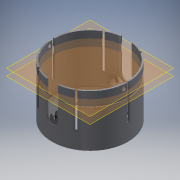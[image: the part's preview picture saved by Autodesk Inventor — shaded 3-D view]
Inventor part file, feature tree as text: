
AUTODESK INVENTOR PART (.ipt)
format: ipt  version: 2016 (Build 200138000, 138)  size: 449,024 bytes
history: native  units: mm
features: sketch x14, extrude x13, reference x8, plane x4, other x2, thicken_offset x2, mirror x1, pattern_circular x1, hole x1
ambient origin geometry x8: Origin, YZ Plane, XZ Plane, XY Plane, X Axis, Y Axis, Z Axis, Center Point
bodies: Solid1 (feature_tree)
feature tree (46):
  extrude  "Extrusion1"  Depth=4.0mm TaperAngle=0.0deg
  extrude  "Extrusion2"  Depth=4.0mm TaperAngle=0.0deg
  sketch  "Sketch3"  dims[d8=4.0mm d9=0.0mm d10=0.0mm d11=0.0mm]
  other  "Work Point1"
  extrude  "Extrusion3"  TaperAngle=0.0deg  [1 undecoded]
  extrude  "Extrusion4"  Depth=0.2mm
  extrude  "Extrusion5"  Depth=2.0mm
  plane  "Work Plane1"
  extrude  "Extrusion6"  Depth=1.0mm
  thicken_offset  "Thicken2"
  thicken_offset  "Thicken3"
  mirror  "Mirror1"
  extrude  "Extrusion7"  [1 undecoded]
  plane  "Work Plane2"
  extrude  "Extrusion8"  Depth=0.523599mm
  sketch  "Sketch9"  dims[d29=50.0mm d30=0.0mm d31=60.0mm d32=360.0deg]
  plane  "Work Plane3"
  plane  "Work Plane4"
  extrude  "Extrusion9"  Depth=60.0mm TaperAngle=360.0deg
  extrude  "Extrusion10"  Depth=50.0mm TaperAngle=0.0deg
  pattern_circular  "Circular Pattern1"  [2 undecoded]
  extrude  "Extrusion11"  Depth=3.0mm
  extrude  "Extrusion12"  Depth=3.0mm
  extrude  "Extrusion13"  Depth=3.0mm
  hole  "Hole1"  [1 undecoded]
  sketch  "Sketch1"  dims[d0=4.0mm d1=0.0mm d2=4.0mm d3=0.0mm]
  reference  "Reference1"
  reference  "Reference2"
  sketch  "Sketch2"  dims[d4=4.0mm d5=0.0mm d6=4.0mm d7=0.0mm]
  reference  "Reference3"
  reference  "Reference4"
  sketch  "Sketch4"  dims[d14=0.2mm d15=0.2mm d16=0.2mm d17=0.2mm]
  sketch  "Sketch5"  dims[d18=4.0mm d19=0.0mm d20=2.0mm]
  reference  "Reference6"
  sketch  "Sketch6"  dims[d21=70.0mm d22=0.0mm d23=1.0mm]
  reference  "Reference7"
  other  "Work Point2"
  sketch  "Sketch7"  dims[d24=-10.0mm d25=-20.0mm]
  sketch  "Sketch8"  dims[d26=70.0mm d27=0.0mm d28=0.523599mm]
  sketch  "Sketch10"  dims[d34=50.0mm d35=0.0mm d36=50.0mm d37=0.0mm]
  sketch  "Sketch11"  dims[d38=3.5mm]
  reference  "Reference8"
  sketch  "Sketch12"  dims[d39=0.0mm d40=0.0mm]
  reference  "Reference9"
  sketch  "Sketch13"  dims[d41=3.0mm]
  sketch  "Sketch14"  dims[d42=3.0mm d43=3.0mm d44=3.0mm d45=3.0mm d46=3.0mm d47=3.0mm d48=3.0mm d49=3.1mm d50=6.0mm d51=4.0mm d52=2.0mm d53=90.0deg d54=6.0mm d55=20.594885mm]
note: 5 required parameter values undecoded (feature->parameter linkage not recoverable at this tier; creation-order binding heuristic only, values carry confidence <= 0.55)
